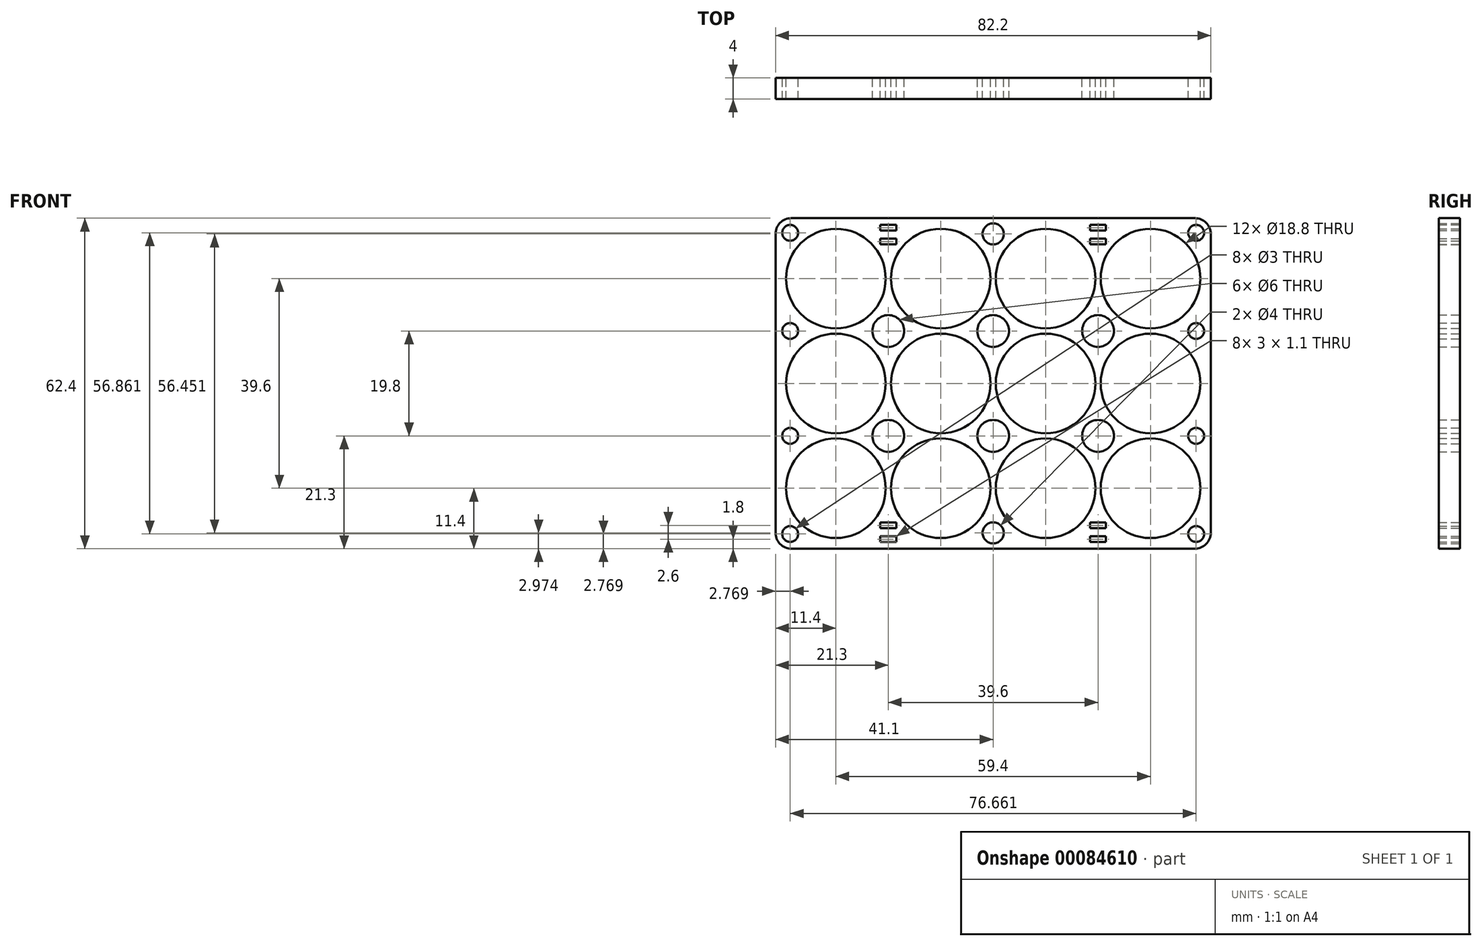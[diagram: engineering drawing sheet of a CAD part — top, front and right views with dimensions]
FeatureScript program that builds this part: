
annotation { "Feature Type Name" : "Feature", "Feature Type Description" : "" }
export const myFeature = defineFeature(function(context is Context, id is Id, definition is map)
    precondition{}
    {
        {
            var Q0;
            Q0=qCreatedBy(makeId("Front.planeOp"),FACE);
            var sketch = newSketch(context, id + "F0", { "sketchPlane" : qUnion([Q0]) });
            skCircle(sketch, "E0", {"center": v(0, 0) * mm, "radius": 9.4 * mm});
            skCircle(sketch, "E1.0.1.0", {"center": v(0, 19.8) * mm, "radius": 9.4 * mm});
            skCircle(sketch, "E1.0.2.0", {"center": v(0, 39.6) * mm, "radius": 9.4 * mm});
            skCircle(sketch, "E1.1.0.0", {"center": v(19.8, 0) * mm, "radius": 9.4 * mm});
            skCircle(sketch, "E1.1.1.0", {"center": v(19.8, 19.8) * mm, "radius": 9.4 * mm});
            skCircle(sketch, "E1.1.2.0", {"center": v(19.8, 39.6) * mm, "radius": 9.4 * mm});
            skCircle(sketch, "E1.2.0.0", {"center": v(39.6, 0) * mm, "radius": 9.4 * mm});
            skCircle(sketch, "E1.2.1.0", {"center": v(39.6, 19.8) * mm, "radius": 9.4 * mm});
            skCircle(sketch, "E1.2.2.0", {"center": v(39.6, 39.6) * mm, "radius": 9.4 * mm});
            skCircle(sketch, "E1.3.0.0", {"center": v(59.4, 0) * mm, "radius": 9.4 * mm});
            skCircle(sketch, "E1.3.1.0", {"center": v(59.4, 19.8) * mm, "radius": 9.4 * mm});
            skCircle(sketch, "E1.3.2.0", {"center": v(59.4, 39.6) * mm, "radius": 9.4 * mm});
            skLineSegment(sketch, "E1.direction1", {"start": v(0, 0) * mm, "end": v(19.8, 0) * mm, "construction": true});
            skLineSegment(sketch, "E1.direction2", {"start": v(0, 0) * mm, "end": v(0, 19.8) * mm, "construction": true});
            skLineSegment(sketch, "E2", {"start": v(-9.4, 19.8) * mm, "end": v(68.8, 19.8) * mm, "construction": true});
            skLineSegment(sketch, "E3", {"start": v(29.7, 19.8) * mm, "end": v(29.7, -16.3) * mm, "construction": true});
            skLineSegment(sketch, "E4.bottom", {"start": v(70.8, -11.4) * mm, "end": v(-11.4, -11.4) * mm});
            skLineSegment(sketch, "E4.top", {"start": v(70.8, 51) * mm, "end": v(-11.4, 51) * mm});
            skLineSegment(sketch, "E4.left", {"start": v(70.8, -11.4) * mm, "end": v(70.8, 51) * mm});
            skLineSegment(sketch, "E4.right", {"start": v(-11.4, -11.4) * mm, "end": v(-11.4, 51) * mm});
            skPoint(sketch, "E4.middle", {"position": v(29.7, 19.8) * mm});
            skLineSegment(sketch, "E5", {"start": v(19.8, 19.8) * mm, "end": v(0, 0) * mm, "construction": true});
            skLineSegment(sketch, "E6", {"start": v(19.8, 0) * mm, "end": v(0, 19.8) * mm, "construction": true});
            skCircle(sketch, "E7", {"center": v(9.9, 9.9) * mm, "radius": 3 * mm});
            skCircle(sketch, "E8.0.1.0", {"center": v(9.9, 29.7) * mm, "radius": 3 * mm});
            skCircle(sketch, "E8.1.0.0", {"center": v(29.7, 9.9) * mm, "radius": 3 * mm});
            skCircle(sketch, "E8.1.1.0", {"center": v(29.7, 29.7) * mm, "radius": 3 * mm});
            skCircle(sketch, "E8.2.0.0", {"center": v(49.5, 9.9) * mm, "radius": 3 * mm});
            skCircle(sketch, "E8.2.1.0", {"center": v(49.5, 29.7) * mm, "radius": 3 * mm});
            skLineSegment(sketch, "E8.direction1", {"start": v(9.9, 9.9) * mm, "end": v(29.7, 9.9) * mm, "construction": true});
            skLineSegment(sketch, "E8.direction2", {"start": v(9.9, 9.9) * mm, "end": v(9.9, 29.7) * mm, "construction": true});
            skLineSegment(sketch, "E9", {"start": v(9.9, 0) * mm, "end": v(9.9, -11.4) * mm, "construction": true});
            skCircle(sketch, "E10.1.0.0", {"center": v(29.7, -8.43) * mm, "radius": 2 * mm});
            skLineSegment(sketch, "E10.direction1", {"start": v(9.9, -8.43) * mm, "end": v(29.7, -8.43) * mm, "construction": true});
            skCircle(sketch, "E11.MirrorC", {"center": v(29.7, 48.03) * mm, "radius": 2 * mm});
            skLineSegment(sketch, "E12", {"start": v(0, 0) * mm, "end": v(-11.4, -11.4) * mm, "construction": true});
            skCircle(sketch, "E13", {"center": v(-8.63, -8.63) * mm, "radius": 1.5 * mm});
            skCircle(sketch, "E14", {"center": v(-8.63, 9.9) * mm, "radius": 1.5 * mm});
            skCircle(sketch, "E15", {"center": v(-8.63, 29.7) * mm, "radius": 1.5 * mm});
            skCircle(sketch, "E16.MirrorC", {"center": v(-8.63, 48.23) * mm, "radius": 1.5 * mm});
            skCircle(sketch, "E17.MirrorC", {"center": v(68.03, -8.63) * mm, "radius": 1.5 * mm});
            skCircle(sketch, "E18.MirrorC", {"center": v(68.03, 9.9) * mm, "radius": 1.5 * mm});
            skCircle(sketch, "E19.MirrorC", {"center": v(68.03, 29.7) * mm, "radius": 1.5 * mm});
            skCircle(sketch, "E20.MirrorC", {"center": v(68.03, 48.23) * mm, "radius": 1.5 * mm});
            skLineSegment(sketch, "E21", {"start": v(9.9, 29.7) * mm, "end": v(9.9, 51) * mm, "construction": true});
            skLineSegment(sketch, "E22.bottom", {"start": v(11.4, 48.65) * mm, "end": v(8.4, 48.65) * mm});
            skLineSegment(sketch, "E22.top", {"start": v(11.4, 49.75) * mm, "end": v(8.4, 49.75) * mm});
            skLineSegment(sketch, "E22.left", {"start": v(11.4, 48.65) * mm, "end": v(11.4, 49.75) * mm});
            skLineSegment(sketch, "E22.right", {"start": v(8.4, 48.65) * mm, "end": v(8.4, 49.75) * mm});
            skPoint(sketch, "E22.middle", {"position": v(9.9, 49.2) * mm});
            skLineSegment(sketch, "E23.bottom", {"start": v(11.4, 46.05) * mm, "end": v(8.4, 46.05) * mm});
            skLineSegment(sketch, "E23.top", {"start": v(11.4, 47.15) * mm, "end": v(8.4, 47.15) * mm});
            skLineSegment(sketch, "E23.left", {"start": v(11.4, 46.05) * mm, "end": v(11.4, 47.15) * mm});
            skLineSegment(sketch, "E23.right", {"start": v(8.4, 46.05) * mm, "end": v(8.4, 47.15) * mm});
            skPoint(sketch, "E23.middle", {"position": v(9.9, 46.6) * mm});
            skLineSegment(sketch, "E24.MirrorCS", {"start": v(8.4, -9.05) * mm, "end": v(8.4, -10.15) * mm});
            skLineSegment(sketch, "E25.MirrorCS", {"start": v(11.4, -10.15) * mm, "end": v(8.4, -10.15) * mm});
            skLineSegment(sketch, "E26.MirrorCS", {"start": v(11.4, -9.05) * mm, "end": v(8.4, -9.05) * mm});
            skLineSegment(sketch, "E27.MirrorCS", {"start": v(11.4, -9.05) * mm, "end": v(11.4, -10.15) * mm});
            skLineSegment(sketch, "E28.MirrorCS", {"start": v(11.4, -7.55) * mm, "end": v(8.4, -7.55) * mm});
            skLineSegment(sketch, "E29.MirrorCS", {"start": v(11.4, -6.45) * mm, "end": v(11.4, -7.55) * mm});
            skLineSegment(sketch, "E30.MirrorCS", {"start": v(11.4, -6.45) * mm, "end": v(8.4, -6.45) * mm});
            skLineSegment(sketch, "E31.MirrorCS", {"start": v(8.4, -6.45) * mm, "end": v(8.4, -7.55) * mm});
            skLineSegment(sketch, "E32.MirrorCS", {"start": v(51, 48.65) * mm, "end": v(51, 49.75) * mm});
            skLineSegment(sketch, "E33.MirrorCS", {"start": v(48, 48.65) * mm, "end": v(48, 49.75) * mm});
            skLineSegment(sketch, "E34.MirrorCS", {"start": v(48, 48.65) * mm, "end": v(51, 48.65) * mm});
            skLineSegment(sketch, "E35.MirrorCS", {"start": v(48, 49.75) * mm, "end": v(51, 49.75) * mm});
            skLineSegment(sketch, "E36.MirrorCS", {"start": v(48, 47.15) * mm, "end": v(51, 47.15) * mm});
            skLineSegment(sketch, "E37.MirrorCS", {"start": v(48, 46.05) * mm, "end": v(51, 46.05) * mm});
            skLineSegment(sketch, "E38.MirrorCS", {"start": v(51, 46.05) * mm, "end": v(51, 47.15) * mm});
            skLineSegment(sketch, "E39.MirrorCS", {"start": v(48, 46.05) * mm, "end": v(48, 47.15) * mm});
            skLineSegment(sketch, "E40.MirrorCS", {"start": v(51, -6.45) * mm, "end": v(51, -7.55) * mm});
            skLineSegment(sketch, "E41.MirrorCS", {"start": v(48, -6.45) * mm, "end": v(48, -7.55) * mm});
            skLineSegment(sketch, "E42.MirrorCS", {"start": v(48, -6.45) * mm, "end": v(51, -6.45) * mm});
            skLineSegment(sketch, "E43.MirrorCS", {"start": v(48, -7.55) * mm, "end": v(51, -7.55) * mm});
            skLineSegment(sketch, "E44.MirrorCS", {"start": v(48, -9.05) * mm, "end": v(51, -9.05) * mm});
            skLineSegment(sketch, "E45.MirrorCS", {"start": v(48, -10.15) * mm, "end": v(51, -10.15) * mm});
            skLineSegment(sketch, "E46.MirrorCS", {"start": v(51, -9.05) * mm, "end": v(51, -10.15) * mm});
            skLineSegment(sketch, "E47.MirrorCS", {"start": v(48, -9.05) * mm, "end": v(48, -10.15) * mm});
            skSolve(sketch);
        }
        {
            var Q0;
            Q0=qSketchRegion(id+"F0",true);
            extrude(context, id + "F1", {"entities" : qUnion([Q0]), "depth" : 4 * mm});
        }
        {
            var Q0;
            Q0=makeQuery(id+"F1.opExtrude","SWEPT_EDGE",EDGE,{"disambiguationData":[OSD([sQuery(id+"F0.wireOp",EDGE,"E4.top"),sQuery(id+"F0.wireOp",EDGE,"E4.left")])]});
            var Q1;
            Q1=makeQuery(id+"F1.opExtrude","SWEPT_EDGE",EDGE,{"disambiguationData":[OSD([sQuery(id+"F0.wireOp",EDGE,"E4.top"),sQuery(id+"F0.wireOp",EDGE,"E4.right")])]});
            var Q2;
            Q2=makeQuery(id+"F1.opExtrude","SWEPT_EDGE",EDGE,{"disambiguationData":[OSD([sQuery(id+"F0.wireOp",EDGE,"E4.bottom"),sQuery(id+"F0.wireOp",EDGE,"E4.right")])]});
            var Q3;
            Q3=makeQuery(id+"F1.opExtrude","SWEPT_EDGE",EDGE,{"disambiguationData":[OSD([sQuery(id+"F0.wireOp",EDGE,"E4.bottom"),sQuery(id+"F0.wireOp",EDGE,"E4.left")])]});
            fillet(context, id + "F2", {"entities" : qUnion([Q0, Q1, Q2, Q3]), "radius" : 3 * mm, "tangentPropagation" : true, "conicFillet" : false});
        }
    });
